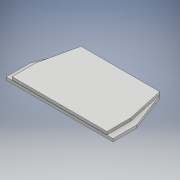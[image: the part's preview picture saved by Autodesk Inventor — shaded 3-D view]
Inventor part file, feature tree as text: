
AUTODESK INVENTOR PART (.ipt)
format: ipt  version: 2018 (Build 220112000, 112)  size: 122,368 bytes
history: native  units: mm
features: extrude x2, sketch x2, pattern_linear x1, projected_geometry x1
ambient origin geometry x8: Origin, YZ Plane, XZ Plane, XY Plane, X Axis, Y Axis, Z Axis, Center Point
bodies: Solid1 (feature_tree)
feature tree (6):
  extrude  "Extrusion1"  Depth=41.0mm
  pattern_linear  "Rectangular Pattern1"  Spacing1=16.0mm  [1 undecoded]
  extrude  "Extrusion2"  Depth=1.94mm TaperAngle=0.0deg
  sketch  "Sketch1"  dims[d0=72.0mm d1=41.0mm]
  sketch  "Sketch2"  dims[d2=53.0mm d3=16.0mm d4=1.94mm d5=0.0mm d6=20.0mm d8=2.1mm d9=64.0mm d10=10.0mm d11=0.0mm]
  projected_geometry  "Projected Loop1"
note: 1 required parameter value undecoded (feature->parameter linkage not recoverable at this tier; creation-order binding heuristic only, values carry confidence <= 0.55)
